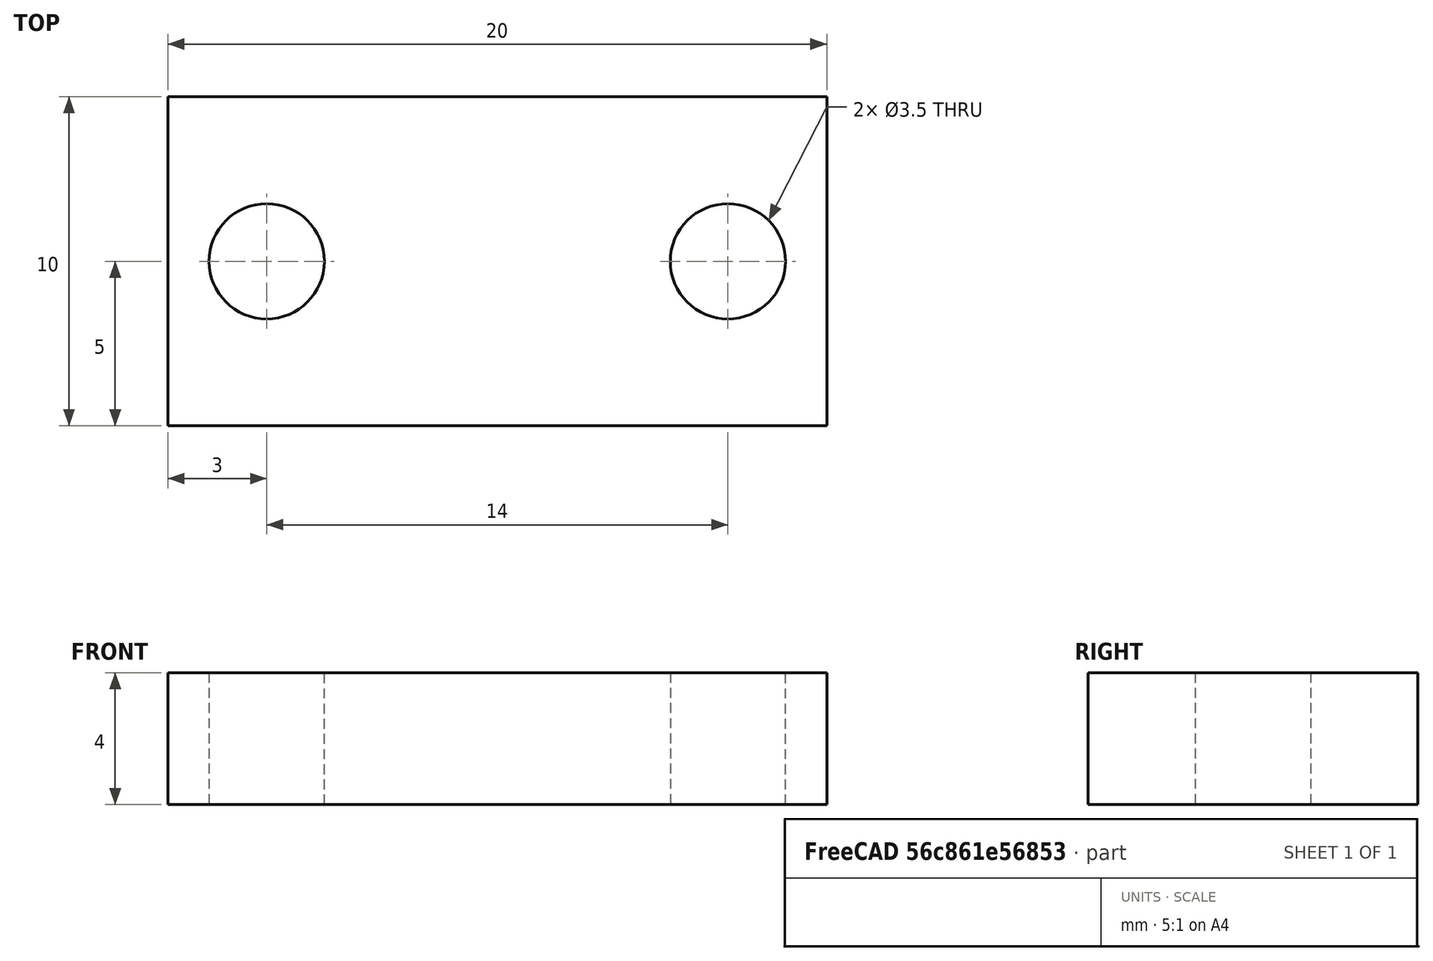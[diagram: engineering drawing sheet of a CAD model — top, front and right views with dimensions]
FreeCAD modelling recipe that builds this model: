
FCSTD DOCUMENT  (FreeCAD 0.20R29410 (Git))
Label: drzac_kabla
License: All rights reserved
LicenseURL: http://en.wikipedia.org/wiki/All_rights_reserved
objects: Sketcher::SketchObject×1, PartDesign::Pad×1, PartDesign::Body×1
note: 4 computed .brp shape members not serialized (recipe doc carries the construction recipe); baked Part::Feature solids carry a one-line shape summary decoded from their .brp

FEATURE [Sketcher::SketchObject] Sketch
  FullyConstrained = true
  MapMode = 5
  Support = -> [XY_Plane]
  sketch-geometry (6):
    g0: LineSegment StartX=-10 StartY=5 StartZ=0 EndX=10 EndY=5 EndZ=0
    g1: LineSegment StartX=10 StartY=5 StartZ=0 EndX=10 EndY=-5 EndZ=0
    g2: LineSegment StartX=10 StartY=-5 StartZ=0 EndX=-10 EndY=-5 EndZ=0
    g3: LineSegment StartX=-10 StartY=-5 StartZ=0 EndX=-10 EndY=5 EndZ=0
    g4: Circle CenterX=-7 CenterY=0 CenterZ=0 NormalX=0 NormalY=0 NormalZ=1 AngleXU=0 Radius=1.75
    g5: Circle CenterX=7 CenterY=0 CenterZ=0 NormalX=0 NormalY=0 NormalZ=1 AngleXU=0 Radius=1.75
  constraints (15):
    c: Coincident(g0,g1)
    c: Coincident(g1,g2)
    c: Coincident(g2,g3)
    c: Coincident(g3,g0)
    c: Horizontal(g0)
    c: Vertical(g3)
    c: Symmetric(g2,g1,g-2)
    c: Symmetric(g1,g0,g-1)
    c: DistanceX(g2,g2) = 20
    c: DistanceY(g1,g1) = 10
    c: PointOnObject(g4,g-1)
    c: Equal(g4,g5)
    c: Symmetric(g4,g5,g-2)
    c: DistanceX(g4,g5) = 14
    c: Diameter(g4) = 3.5
FEATURE [PartDesign::Pad] Pad
  Direction = (0,0,1)
  Length = 4
  Length2 = 10
  Profile = -> Sketch
  ReferenceAxis = -> Sketch [N_Axis]
  Type = 0
FEATURE [PartDesign::Body] Body
  Group = -> [Sketch,Pad]
  Origin = -> Origin
  Tip = -> Pad
